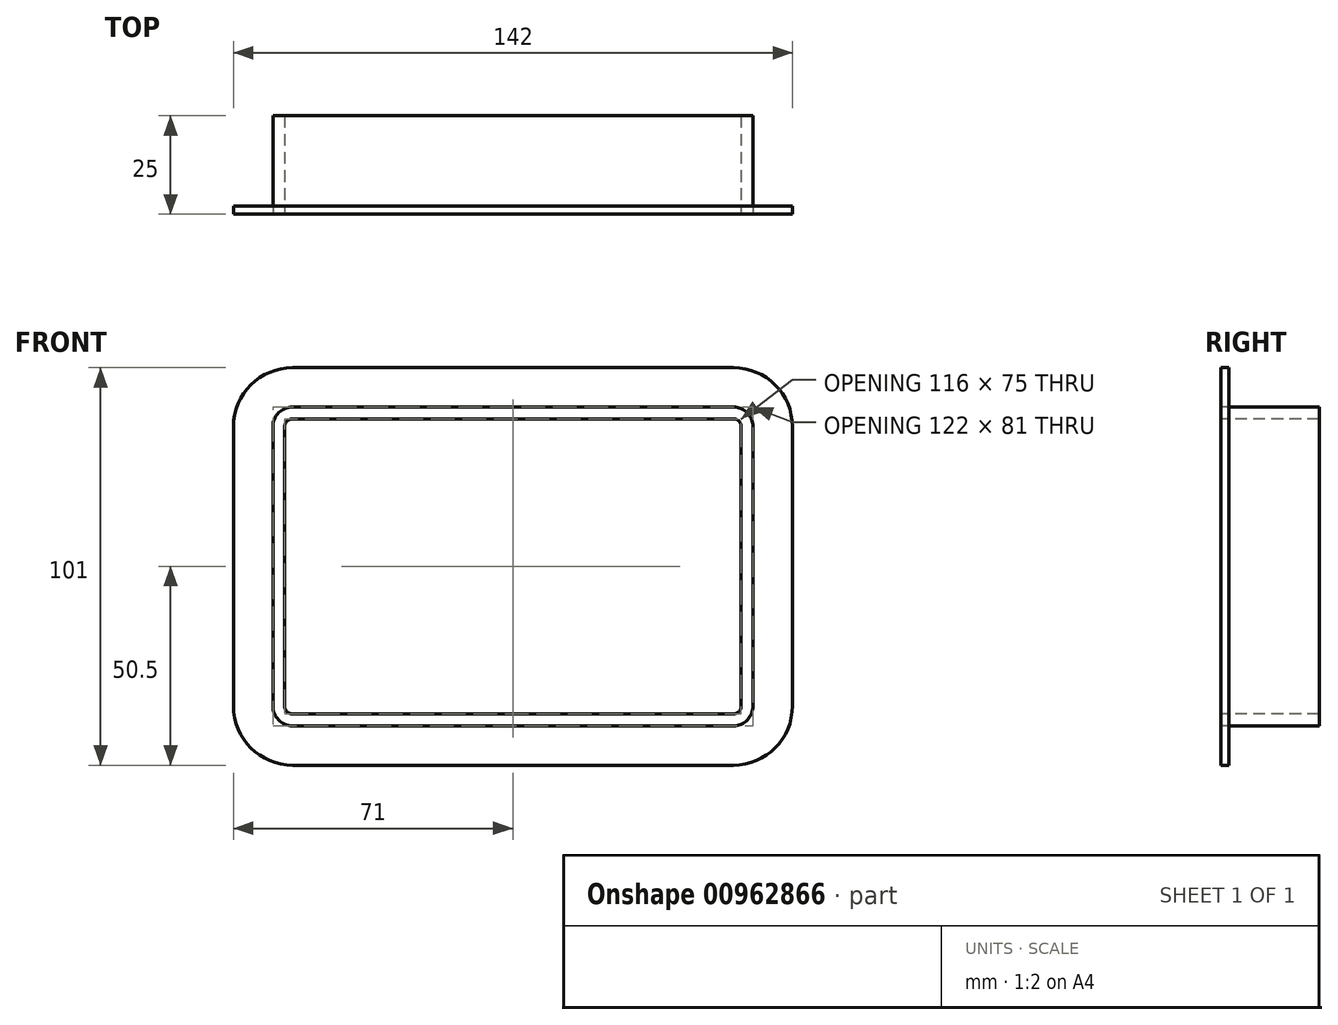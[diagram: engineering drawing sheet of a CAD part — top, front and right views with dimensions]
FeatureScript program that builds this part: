
annotation { "Feature Type Name" : "Feature", "Feature Type Description" : "" }
export const myFeature = defineFeature(function(context is Context, id is Id, definition is map)
    precondition{}
    {
        {
            var Q0;
            Q0=qCreatedBy(makeId("Front.planeOp"),FACE);
            var sketch = newSketch(context, id + "F0", { "sketchPlane" : qUnion([Q0])});
            skLineSegment(sketch, "E0.bottom", {"start": v(5, 0) * mm, "end": v(117, 0) * mm});
            skLineSegment(sketch, "E0.top", {"start": v(5, 81) * mm, "end": v(117, 81) * mm});
            skLineSegment(sketch, "E0.left", {"start": v(0, 5) * mm, "end": v(0, 76) * mm});
            skLineSegment(sketch, "E0.right", {"start": v(122, 5) * mm, "end": v(122, 76) * mm});
            skPoint(sketch, "E1.visualSharp", {"position": v(0, 81) * mm});
            skArc(sketch, "E1.filletArc", {"start": v(5, 81) * mm, "mid": v(1.46, 79.54) * mm, "end": v(0, 76) * mm});
            skPoint(sketch, "E2.visualSharp", {"position": v(122, 81) * mm});
            skArc(sketch, "E2.filletArc", {"start": v(122, 76) * mm, "mid": v(120.54, 79.54) * mm, "end": v(117, 81) * mm});
            skPoint(sketch, "E3.visualSharp", {"position": v(122, 0) * mm});
            skArc(sketch, "E3.filletArc", {"start": v(117, 0) * mm, "mid": v(120.54, 1.46) * mm, "end": v(122, 5) * mm});
            skPoint(sketch, "E4.visualSharp", {"position": v(0, 0) * mm});
            skArc(sketch, "E4.filletArc", {"start": v(0, 5) * mm, "mid": v(1.46, 1.46) * mm, "end": v(5, 0) * mm});
            skLineSegment(sketch, "E5.0", {"start": v(5, 91) * mm, "end": v(117, 91) * mm});
            skLineSegment(sketch, "E6.0", {"start": v(-10, 5) * mm, "end": v(-10, 76) * mm});
            skLineSegment(sketch, "E7.0", {"start": v(5, -10) * mm, "end": v(117, -10) * mm});
            skLineSegment(sketch, "E8.0", {"start": v(132, 5) * mm, "end": v(132, 76) * mm});
            skArc(sketch, "E9.0", {"start": v(5, 91) * mm, "mid": v(-5.6, 86.6) * mm, "end": v(-10, 76) * mm});
            skArc(sketch, "E10.0", {"start": v(-10, 5) * mm, "mid": v(-5.6, -5.6) * mm, "end": v(5, -10) * mm});
            skArc(sketch, "E11.0", {"start": v(117, -10) * mm, "mid": v(127.6, -5.6) * mm, "end": v(132, 5) * mm});
            skArc(sketch, "E12.0", {"start": v(132, 76) * mm, "mid": v(127.6, 86.6) * mm, "end": v(117, 91) * mm});
            skSolve(sketch);
        }
        {
            var Q0;
            Q0=makeQuery(id+"F0.imprint","IMPRINT",FACE,{"disambiguationData":[TD([[makeQuery(id+"F0.imprint","IMPRINT",EDGE,{"derivedFrom":sQuery(id+"F0.wireOp",EDGE,"E0.bottom")}),-1.0]])]});
            extrude(context, id + "F1", {"entities" : qUnion([Q0]), "depth" : 2 * mm, "offsetDistance" : 25 * mm});
        }
        {
            var Q0;
            Q0=makeQuery(id+"F1.opExtrude","CAP_FACE",FACE,{"disambiguationData":[OSD([sQuery(id+"F0.wireOp",EDGE,"E0.bottom"),sQuery(id+"F0.wireOp",EDGE,"E0.top"),sQuery(id+"F0.wireOp",EDGE,"E0.left"),sQuery(id+"F0.wireOp",EDGE,"E0.right"),sQuery(id+"F0.wireOp",EDGE,"E1.filletArc"),sQuery(id+"F0.wireOp",EDGE,"E2.filletArc"),sQuery(id+"F0.wireOp",EDGE,"E3.filletArc"),sQuery(id+"F0.wireOp",EDGE,"E4.filletArc"),sQuery(id+"F0.wireOp",EDGE,"E5.0"),sQuery(id+"F0.wireOp",EDGE,"E6.0"),sQuery(id+"F0.wireOp",EDGE,"E7.0"),sQuery(id+"F0.wireOp",EDGE,"E8.0"),sQuery(id+"F0.wireOp",EDGE,"E9.0"),sQuery(id+"F0.wireOp",EDGE,"E10.0"),sQuery(id+"F0.wireOp",EDGE,"E11.0"),sQuery(id+"F0.wireOp",EDGE,"E12.0")])],"isStart":false});
            var sketch = newSketch(context, id + "F2", { "sketchPlane" : qUnion([Q0])});
            skLineSegment(sketch, "E13.0", {"start": v(5, 81) * mm, "end": v(117, 81) * mm});
            skPoint(sketch, "E14.0", {"position": v(1.46, 79.54) * mm});
            skPoint(sketch, "E15.0", {"position": v(0, 76) * mm});
            skArc(sketch, "E16.0", {"start": v(5, 81) * mm, "mid": v(1.46, 79.54) * mm, "end": v(0, 76) * mm});
            skLineSegment(sketch, "E17.0", {"start": v(0, 5) * mm, "end": v(0, 76) * mm});
            skArc(sketch, "E18.0", {"start": v(0, 5) * mm, "mid": v(1.46, 1.46) * mm, "end": v(5, 0) * mm});
            skLineSegment(sketch, "E19.0", {"start": v(5, 0) * mm, "end": v(117, 0) * mm});
            skArc(sketch, "E20.0", {"start": v(117, 0) * mm, "mid": v(120.54, 1.46) * mm, "end": v(122, 5) * mm});
            skLineSegment(sketch, "E21.0", {"start": v(122, 5) * mm, "end": v(122, 76) * mm});
            skArc(sketch, "E22.0", {"start": v(122, 76) * mm, "mid": v(120.54, 79.54) * mm, "end": v(117, 81) * mm});
            skLineSegment(sketch, "E23.0", {"start": v(5, 78) * mm, "end": v(117, 78) * mm});
            skArc(sketch, "E24.0", {"start": v(5, 78) * mm, "mid": v(3.59, 77.41) * mm, "end": v(3, 76) * mm});
            skLineSegment(sketch, "E25.0", {"start": v(3, 5) * mm, "end": v(3, 76) * mm});
            skLineSegment(sketch, "E26.0", {"start": v(5, 3) * mm, "end": v(117, 3) * mm});
            skArc(sketch, "E27.0", {"start": v(3, 5) * mm, "mid": v(3.59, 3.59) * mm, "end": v(5, 3) * mm});
            skLineSegment(sketch, "E28.0", {"start": v(119, 5) * mm, "end": v(119, 76) * mm});
            skArc(sketch, "E29.0", {"start": v(117, 3) * mm, "mid": v(118.41, 3.59) * mm, "end": v(119, 5) * mm});
            skArc(sketch, "E30.0", {"start": v(119, 76) * mm, "mid": v(118.41, 77.41) * mm, "end": v(117, 78) * mm});
            skSolve(sketch);
        }
        {
            var Q0;
            Q0=makeQuery(id+"F2.imprint","IMPRINT",FACE,{"disambiguationData":[TD([[makeQuery(id+"F2.imprint","IMPRINT",EDGE,{"derivedFrom":sQuery(id+"F2.wireOp",EDGE,"E13.0")}),-1.0]])]});
            extrude(context, id + "F3", {"entities" : qUnion([Q0]), "oppositeDirection" : true, "depth" : 25 * mm, "offsetDistance" : 25 * mm});
        }
    });
